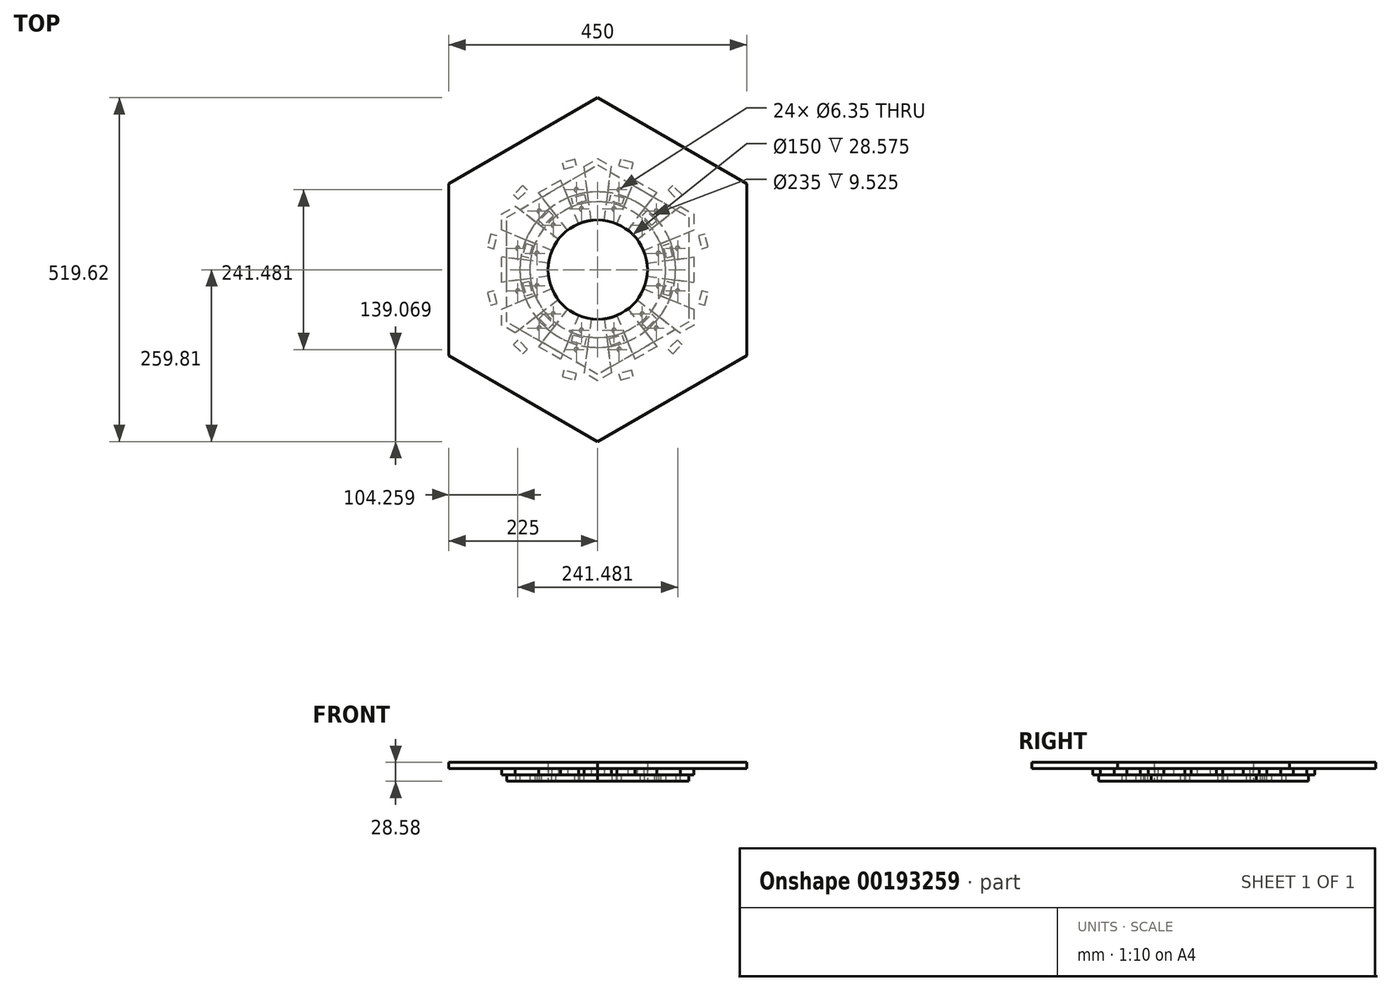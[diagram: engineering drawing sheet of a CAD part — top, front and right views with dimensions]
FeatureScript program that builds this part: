
annotation { "Feature Type Name" : "Feature", "Feature Type Description" : "" }
export const myFeature = defineFeature(function(context is Context, id is Id, definition is map)
    precondition{}
    {
        {
            var Q0;
            Q0=qCreatedBy(makeId("Top.planeOp"),FACE);
            var sketch = newSketch(context, id + "F0", { "sketchPlane" : qUnion([Q0])});
            skCircle(sketch, "E0.cCircle", {"center": v(0, 0) * mm, "radius": 158.5 * mm, "construction": true});
            skLineSegment(sketch, "E0.0", {"start": v(0, 158.5) * mm, "end": v(137.27, 79.25) * mm});
            skLineSegment(sketch, "E0.1", {"start": v(137.27, 79.25) * mm, "end": v(137.27, -79.25) * mm});
            skLineSegment(sketch, "E0.2", {"start": v(137.27, -79.25) * mm, "end": v(0, -158.5) * mm});
            skLineSegment(sketch, "E0.3", {"start": v(0, -158.5) * mm, "end": v(-137.27, -79.25) * mm});
            skLineSegment(sketch, "E0.4", {"start": v(-137.27, -79.25) * mm, "end": v(-137.27, 79.25) * mm});
            skLineSegment(sketch, "E0.5", {"start": v(-137.27, 79.25) * mm, "end": v(0, 158.5) * mm});
            skCircle(sketch, "E1", {"center": v(0, 0) * mm, "radius": 75 * mm});
            skLineSegment(sketch, "E2", {"start": v(0, 0) * mm, "end": v(0, 158.5) * mm});
            skLineSegment(sketch, "E3", {"start": v(0, 0) * mm, "end": v(24.59, 91.76) * mm});
            skLineSegment(sketch, "E4", {"start": v(32.35, 120.74) * mm, "end": v(24.59, 91.76) * mm});
            skCircle(sketch, "E5", {"center": v(24.59, 91.76) * mm, "radius": 3.18 * mm});
            skCircle(sketch, "E6", {"center": v(32.35, 120.74) * mm, "radius": 3.18 * mm});
            skCircle(sketch, "E7.1.0", {"center": v(-24.59, 91.76) * mm, "radius": 3.18 * mm});
            skCircle(sketch, "E7.1.1", {"center": v(-32.35, 120.74) * mm, "radius": 3.18 * mm});
            skCircle(sketch, "E7.2.0", {"center": v(-67.18, 67.18) * mm, "radius": 3.18 * mm});
            skCircle(sketch, "E7.2.1", {"center": v(-88.39, 88.39) * mm, "radius": 3.18 * mm});
            skCircle(sketch, "E7.3.0", {"center": v(-91.76, 24.59) * mm, "radius": 3.18 * mm});
            skCircle(sketch, "E7.3.1", {"center": v(-120.74, 32.35) * mm, "radius": 3.18 * mm});
            skCircle(sketch, "E7.4.0", {"center": v(-91.76, -24.59) * mm, "radius": 3.18 * mm});
            skCircle(sketch, "E7.4.1", {"center": v(-120.74, -32.35) * mm, "radius": 3.18 * mm});
            skCircle(sketch, "E7.5.0", {"center": v(-67.18, -67.18) * mm, "radius": 3.18 * mm});
            skCircle(sketch, "E7.5.1", {"center": v(-88.39, -88.39) * mm, "radius": 3.18 * mm});
            skCircle(sketch, "E7.6.0", {"center": v(-24.59, -91.76) * mm, "radius": 3.18 * mm});
            skCircle(sketch, "E7.6.1", {"center": v(-32.35, -120.74) * mm, "radius": 3.18 * mm});
            skCircle(sketch, "E7.7.0", {"center": v(24.59, -91.76) * mm, "radius": 3.18 * mm});
            skCircle(sketch, "E7.7.1", {"center": v(32.35, -120.74) * mm, "radius": 3.18 * mm});
            skCircle(sketch, "E7.8.0", {"center": v(67.18, -67.18) * mm, "radius": 3.18 * mm});
            skCircle(sketch, "E7.8.1", {"center": v(88.39, -88.39) * mm, "radius": 3.18 * mm});
            skCircle(sketch, "E7.9.0", {"center": v(91.76, -24.59) * mm, "radius": 3.18 * mm});
            skCircle(sketch, "E7.9.1", {"center": v(120.74, -32.35) * mm, "radius": 3.18 * mm});
            skCircle(sketch, "E7.10.0", {"center": v(91.76, 24.59) * mm, "radius": 3.18 * mm});
            skCircle(sketch, "E7.10.1", {"center": v(120.74, 32.35) * mm, "radius": 3.18 * mm});
            skCircle(sketch, "E7.11.0", {"center": v(67.18, 67.18) * mm, "radius": 3.18 * mm});
            skCircle(sketch, "E7.11.1", {"center": v(88.39, 88.39) * mm, "radius": 3.18 * mm});
            skSolve(sketch);
        }
        {
            var Q0;
            Q0 = qSketchRegion(id + "F0", true);
            extrude(context, id + "F1", {"entities" : qUnion([Q0]), "depth" : 9.53 * mm});
        }
        {
            var Q0;
            Q0=makeQuery(id+"F1.opExtrude","CAP_FACE",FACE,{"disambiguationData":[OSD([sQuery(id+"F0.wireOp",EDGE,"E0.0"),sQuery(id+"F0.wireOp",EDGE,"E0.1"),sQuery(id+"F0.wireOp",EDGE,"E0.2"),sQuery(id+"F0.wireOp",EDGE,"E0.3"),sQuery(id+"F0.wireOp",EDGE,"E0.4"),sQuery(id+"F0.wireOp",EDGE,"E0.5"),sQuery(id+"F0.wireOp",EDGE,"RleesNmM-tFlp-8cQn-oHbe-ywBhveo3HyHZ")])],"isStart":false});
            var sketch = newSketch(context, id + "F2", { "sketchPlane" : qUnion([Q0])});
            skCircle(sketch, "E8.cCircle", {"center": v(0, 0) * mm, "radius": 167.74 * mm, "construction": true});
            skLineSegment(sketch, "E8.0", {"start": v(145.27, -83.87) * mm, "end": v(0, -167.74) * mm});
            skLineSegment(sketch, "E8.1", {"start": v(0, -167.74) * mm, "end": v(-145.27, -83.87) * mm});
            skLineSegment(sketch, "E8.2", {"start": v(-145.27, -83.87) * mm, "end": v(-145.27, 83.87) * mm});
            skLineSegment(sketch, "E8.3", {"start": v(-145.27, 83.87) * mm, "end": v(0, 167.74) * mm});
            skLineSegment(sketch, "E8.4", {"start": v(0, 167.74) * mm, "end": v(145.27, 83.87) * mm});
            skLineSegment(sketch, "E8.5", {"start": v(145.27, 83.87) * mm, "end": v(145.27, -83.87) * mm});
            skLineSegment(sketch, "E9", {"start": v(0, 0) * mm, "end": v(167.74, 0) * mm});
            skLineSegment(sketch, "E10", {"start": v(0, 0) * mm, "end": v(166.3, -21.9) * mm});
            skLineSegment(sketch, "E11.1.0", {"start": v(0, 0) * mm, "end": v(166.3, 21.9) * mm});
            skLineSegment(sketch, "E11.2.0", {"start": v(0, 0) * mm, "end": v(154.97, 64.2) * mm});
            skLineSegment(sketch, "E11.3.0", {"start": v(0, 0) * mm, "end": v(133.08, 102.11) * mm});
            skLineSegment(sketch, "E11.4.0", {"start": v(0, 0) * mm, "end": v(102.11, 133.08) * mm});
            skLineSegment(sketch, "E11.5.0", {"start": v(0, 0) * mm, "end": v(64.2, 154.97) * mm});
            skLineSegment(sketch, "E11.7.0", {"start": v(0, 0) * mm, "end": v(-21.9, 166.3) * mm});
            skLineSegment(sketch, "E11.8.0", {"start": v(0, 0) * mm, "end": v(-64.2, 154.97) * mm});
            skLineSegment(sketch, "E11.9.0", {"start": v(0, 0) * mm, "end": v(-102.11, 133.08) * mm});
            skLineSegment(sketch, "E11.10.0", {"start": v(0, 0) * mm, "end": v(-133.08, 102.11) * mm});
            skLineSegment(sketch, "E11.11.0", {"start": v(0, 0) * mm, "end": v(-154.97, 64.2) * mm});
            skLineSegment(sketch, "E11.12.0", {"start": v(0, 0) * mm, "end": v(-166.3, 21.9) * mm});
            skLineSegment(sketch, "E11.13.0", {"start": v(0, 0) * mm, "end": v(-166.3, -21.9) * mm});
            skLineSegment(sketch, "E11.14.0", {"start": v(0, 0) * mm, "end": v(-154.97, -64.2) * mm});
            skLineSegment(sketch, "E11.15.0", {"start": v(0, 0) * mm, "end": v(-133.08, -102.11) * mm});
            skLineSegment(sketch, "E11.16.0", {"start": v(0, 0) * mm, "end": v(-102.11, -133.08) * mm});
            skLineSegment(sketch, "E11.17.0", {"start": v(0, 0) * mm, "end": v(-64.2, -154.97) * mm});
            skLineSegment(sketch, "E11.18.0", {"start": v(0, 0) * mm, "end": v(-21.9, -166.3) * mm});
            skLineSegment(sketch, "E11.19.0", {"start": v(0, 0) * mm, "end": v(21.9, -166.3) * mm});
            skLineSegment(sketch, "E11.20.0", {"start": v(0, 0) * mm, "end": v(64.2, -154.97) * mm});
            skLineSegment(sketch, "E11.21.0", {"start": v(0, 0) * mm, "end": v(102.11, -133.08) * mm});
            skLineSegment(sketch, "E11.22.0", {"start": v(0, 0) * mm, "end": v(133.08, -102.11) * mm});
            skLineSegment(sketch, "E11.23.0", {"start": v(0, 0) * mm, "end": v(154.97, -64.2) * mm});
            skCircle(sketch, "E12", {"center": v(0, 0) * mm, "radius": 75 * mm});
            skLineSegment(sketch, "E13", {"start": v(0, 0) * mm, "end": v(20.52, 155.89) * mm});
            skSolve(sketch);
        }
        {
            var Q0;
            {var subQ0=sQuery(id+"F2.wireOp",EDGE,"E11.5.0");var subQ1=sQuery(id+"F2.wireOp",EDGE,"E8.4");var subQ2=makeQuery(id+"F2.imprint","INTERSECT",VERTEX,{"derivedFrom":[subQ1,subQ0]});Q0=makeQuery(id+"F2.imprint","IMPRINT",FACE,{"disambiguationData":[TD([[makeQuery(id+"F2.imprint","IMPRINT",EDGE,{"disambiguationData":[TD([[subQ2,-1.0]])],"derivedFrom":subQ1}),-1.0]])]});}
            var Q1;
            {var subQ1=sQuery(id+"F2.wireOp",EDGE,"E8.3");var subQ6=sQuery(id+"F2.wireOp",EDGE,"E8.4");var subQ10=makeQuery(id+"F2.imprint","INTERSECT",VERTEX,{"derivedFrom":[subQ1,subQ6]});Q1=makeQuery(id+"F2.imprint","IMPRINT",FACE,{"disambiguationData":[TD([[makeQuery(id+"F2.imprint","IMPRINT",EDGE,{"disambiguationData":[TD([[subQ10,1.0]])],"derivedFrom":subQ1}),-1.0]])]});}
            var Q2;
            {var subQ0=sQuery(id+"F2.wireOp",EDGE,"E11.13.0");var subQ1=sQuery(id+"F2.wireOp",EDGE,"E8.2");var subQ2=makeQuery(id+"F2.imprint","INTERSECT",VERTEX,{"derivedFrom":[subQ1,subQ0]});Q2=makeQuery(id+"F2.imprint","IMPRINT",FACE,{"disambiguationData":[TD([[makeQuery(id+"F2.imprint","IMPRINT",EDGE,{"disambiguationData":[TD([[subQ2,-1.0]])],"derivedFrom":subQ1}),-1.0]])]});}
            var Q3;
            {var subQ1=sQuery(id+"F2.wireOp",EDGE,"E8.1");var subQ6=sQuery(id+"F2.wireOp",EDGE,"E8.2");var subQ10=makeQuery(id+"F2.imprint","INTERSECT",VERTEX,{"derivedFrom":[subQ1,subQ6]});Q3=makeQuery(id+"F2.imprint","IMPRINT",FACE,{"disambiguationData":[TD([[makeQuery(id+"F2.imprint","IMPRINT",EDGE,{"disambiguationData":[TD([[subQ10,1.0]])],"derivedFrom":subQ1}),-1.0]])]});}
            var Q4;
            {var subQ1=sQuery(id+"F2.wireOp",EDGE,"E8.0");var subQ6=sQuery(id+"F2.wireOp",EDGE,"E8.1");var subQ10=makeQuery(id+"F2.imprint","INTERSECT",VERTEX,{"derivedFrom":[subQ1,subQ6]});Q4=makeQuery(id+"F2.imprint","IMPRINT",FACE,{"disambiguationData":[TD([[makeQuery(id+"F2.imprint","IMPRINT",EDGE,{"disambiguationData":[TD([[subQ10,1.0]])],"derivedFrom":subQ1}),-1.0]])]});}
            var Q5;
            {var subQ0=sQuery(id+"F2.wireOp",EDGE,"E11.21.0");var subQ1=sQuery(id+"F2.wireOp",EDGE,"E8.0");var subQ2=makeQuery(id+"F2.imprint","INTERSECT",VERTEX,{"derivedFrom":[subQ1,subQ0]});Q5=makeQuery(id+"F2.imprint","IMPRINT",FACE,{"disambiguationData":[TD([[makeQuery(id+"F2.imprint","IMPRINT",EDGE,{"disambiguationData":[TD([[subQ2,-1.0]])],"derivedFrom":subQ1}),-1.0]])]});}
            var Q6;
            {var subQ1=sQuery(id+"F2.wireOp",EDGE,"E8.5");var subQ8=sQuery(id+"F2.wireOp",EDGE,"E8.0");var subQ11=makeQuery(id+"F2.imprint","INTERSECT",VERTEX,{"derivedFrom":[subQ8,subQ1]});Q6=makeQuery(id+"F2.imprint","IMPRINT",FACE,{"disambiguationData":[TD([[makeQuery(id+"F2.imprint","IMPRINT",EDGE,{"disambiguationData":[TD([[subQ11,-1.0]])],"derivedFrom":subQ8}),-1.0]])]});}
            var Q7;
            {var subQ1=sQuery(id+"F2.wireOp",EDGE,"E8.4");var subQ6=sQuery(id+"F2.wireOp",EDGE,"E8.5");var subQ10=makeQuery(id+"F2.imprint","INTERSECT",VERTEX,{"derivedFrom":[subQ1,subQ6]});Q7=makeQuery(id+"F2.imprint","IMPRINT",FACE,{"disambiguationData":[TD([[makeQuery(id+"F2.imprint","IMPRINT",EDGE,{"disambiguationData":[TD([[subQ10,1.0]])],"derivedFrom":subQ1}),-1.0]])]});}
            var Q8;
            {var subQ0=sQuery(id+"F2.wireOp",EDGE,"E11.5.0");var subQ1=sQuery(id+"F2.wireOp",EDGE,"E8.4");var subQ2=makeQuery(id+"F2.imprint","INTERSECT",VERTEX,{"derivedFrom":[subQ1,subQ0]});Q8=makeQuery(id+"F2.imprint","IMPRINT",FACE,{"disambiguationData":[TD([[makeQuery(id+"F2.imprint","IMPRINT",EDGE,{"disambiguationData":[TD([[subQ2,-1.0]])],"derivedFrom":subQ1}),-1.0]])]});}
            var Q9;
            {var subQ1=sQuery(id+"F2.wireOp",EDGE,"E8.3");var subQ5=sQuery(id+"F2.wireOp",EDGE,"E8.2");var subQ6=makeQuery(id+"F2.imprint","INTERSECT",VERTEX,{"derivedFrom":[subQ5,subQ1]});Q9=makeQuery(id+"F2.imprint","IMPRINT",FACE,{"disambiguationData":[TD([[makeQuery(id+"F2.imprint","IMPRINT",EDGE,{"disambiguationData":[TD([[subQ6,1.0]])],"derivedFrom":subQ5}),-1.0]])]});}
            var Q10;
            {var subQ5=sQuery(id+"F2.wireOp",EDGE,"E12");var subQ6=sQuery(id+"F2.wireOp",EDGE,"E11.10.0");var subQ7=makeQuery(id+"F2.imprint","INTERSECT",VERTEX,{"derivedFrom":[subQ6,subQ5]});Q10=makeQuery(id+"F2.imprint","IMPRINT",FACE,{"disambiguationData":[TD([[makeQuery(id+"F2.imprint","IMPRINT",EDGE,{"disambiguationData":[TD([[subQ7,-1.0]])],"derivedFrom":subQ6}),1.0]])]});}
            var Q11;
            {var subQ3=sQuery(id+"F2.wireOp",EDGE,"E11.6.0");var subQ5=sQuery(id+"F2.wireOp",EDGE,"E12");var subQ6=makeQuery(id+"F2.imprint","INTERSECT",VERTEX,{"derivedFrom":[subQ3,subQ5]});Q11=makeQuery(id+"F2.imprint","IMPRINT",FACE,{"disambiguationData":[TD([[makeQuery(id+"F2.imprint","IMPRINT",EDGE,{"disambiguationData":[TD([[subQ6,-1.0]])],"derivedFrom":subQ3}),1.0]])]});}
            var Q12;
            {var subQ0=sQuery(id+"F2.wireOp",EDGE,"E11.5.0");var subQ1=sQuery(id+"F2.wireOp",EDGE,"E8.4");var subQ2=makeQuery(id+"F2.imprint","INTERSECT",VERTEX,{"derivedFrom":[subQ1,subQ0]});Q12=makeQuery(id+"F2.imprint","IMPRINT",FACE,{"disambiguationData":[TD([[makeQuery(id+"F2.imprint","IMPRINT",EDGE,{"disambiguationData":[TD([[subQ2,-1.0]])],"derivedFrom":subQ1}),-1.0]])]});}
            var Q13;
            {var subQ0=sQuery(id+"F2.wireOp",EDGE,"E12");var subQ1=sQuery(id+"F2.wireOp",EDGE,"E11.4.0");var subQ2=makeQuery(id+"F2.imprint","INTERSECT",VERTEX,{"derivedFrom":[subQ1,subQ0]});Q13=makeQuery(id+"F2.imprint","IMPRINT",FACE,{"disambiguationData":[TD([[makeQuery(id+"F2.imprint","IMPRINT",EDGE,{"disambiguationData":[TD([[subQ2,-1.0]])],"derivedFrom":subQ1}),1.0]])]});}
            var Q14;
            {var subQ0=sQuery(id+"F2.wireOp",EDGE,"E11.4.0");var subQ1=makeQuery(id+"F1.opExtrude","CAP_EDGE",EDGE,{"disambiguationData":[OSD([sQuery(id+"F0.wireOp",EDGE,"ad7bd027-b6ec-4049-bcbc-d832936b2ed7.0")])],"isStart":false});var subQ2=makeQuery(id+"F2.imprint","INTERSECT",VERTEX,{"derivedFrom":[subQ1,subQ0]});Q14=makeQuery(id+"F2.imprint","IMPRINT",FACE,{"disambiguationData":[TD([[makeQuery(id+"F2.imprint","IMPRINT",EDGE,{"disambiguationData":[TD([[subQ2,-1.0]])],"derivedFrom":subQ0}),1.0]])]});}
            var Q15;
            {var subQ5=sQuery(id+"F2.wireOp",EDGE,"E12");var subQ6=sQuery(id+"F2.wireOp",EDGE,"E11.2.0");var subQ7=makeQuery(id+"F2.imprint","INTERSECT",VERTEX,{"derivedFrom":[subQ6,subQ5]});Q15=makeQuery(id+"F2.imprint","IMPRINT",FACE,{"disambiguationData":[TD([[makeQuery(id+"F2.imprint","IMPRINT",EDGE,{"disambiguationData":[TD([[subQ7,-1.0]])],"derivedFrom":subQ6}),1.0]])]});}
            var Q16;
            {var subQ5=sQuery(id+"F2.wireOp",EDGE,"E12");var subQ6=sQuery(id+"F2.wireOp",EDGE,"E11.22.0");var subQ7=makeQuery(id+"F2.imprint","INTERSECT",VERTEX,{"derivedFrom":[subQ6,subQ5]});Q16=makeQuery(id+"F2.imprint","IMPRINT",FACE,{"disambiguationData":[TD([[makeQuery(id+"F2.imprint","IMPRINT",EDGE,{"disambiguationData":[TD([[subQ7,-1.0]])],"derivedFrom":subQ6}),1.0]])]});}
            var Q17;
            {var subQ0=sQuery(id+"F2.wireOp",EDGE,"E11.21.0");var subQ1=sQuery(id+"F2.wireOp",EDGE,"E8.0");var subQ2=makeQuery(id+"F2.imprint","INTERSECT",VERTEX,{"derivedFrom":[subQ1,subQ0]});Q17=makeQuery(id+"F2.imprint","IMPRINT",FACE,{"disambiguationData":[TD([[makeQuery(id+"F2.imprint","IMPRINT",EDGE,{"disambiguationData":[TD([[subQ2,-1.0]])],"derivedFrom":subQ1}),-1.0]])]});}
            var Q18;
            {var subQ0=sQuery(id+"F2.wireOp",EDGE,"E12");var subQ1=sQuery(id+"F2.wireOp",EDGE,"E11.20.0");var subQ2=makeQuery(id+"F2.imprint","INTERSECT",VERTEX,{"derivedFrom":[subQ1,subQ0]});Q18=makeQuery(id+"F2.imprint","IMPRINT",FACE,{"disambiguationData":[TD([[makeQuery(id+"F2.imprint","IMPRINT",EDGE,{"disambiguationData":[TD([[subQ2,-1.0]])],"derivedFrom":subQ1}),1.0]])]});}
            var Q19;
            {var subQ0=sQuery(id+"F2.wireOp",EDGE,"E11.20.0");var subQ1=makeQuery(id+"F1.opExtrude","CAP_EDGE",EDGE,{"disambiguationData":[OSD([sQuery(id+"F0.wireOp",EDGE,"ad7bd027-b6ec-4049-bcbc-d832936b2ed7.2")])],"isStart":false});var subQ2=makeQuery(id+"F2.imprint","INTERSECT",VERTEX,{"derivedFrom":[subQ1,subQ0]});Q19=makeQuery(id+"F2.imprint","IMPRINT",FACE,{"disambiguationData":[TD([[makeQuery(id+"F2.imprint","IMPRINT",EDGE,{"disambiguationData":[TD([[subQ2,-1.0]])],"derivedFrom":subQ0}),1.0]])]});}
            var Q20;
            {var subQ5=sQuery(id+"F2.wireOp",EDGE,"E12");var subQ6=sQuery(id+"F2.wireOp",EDGE,"E11.18.0");var subQ7=makeQuery(id+"F2.imprint","INTERSECT",VERTEX,{"derivedFrom":[subQ6,subQ5]});Q20=makeQuery(id+"F2.imprint","IMPRINT",FACE,{"disambiguationData":[TD([[makeQuery(id+"F2.imprint","IMPRINT",EDGE,{"disambiguationData":[TD([[subQ7,-1.0]])],"derivedFrom":subQ6}),1.0]])]});}
            var Q21;
            {var subQ5=sQuery(id+"F2.wireOp",EDGE,"E12");var subQ6=sQuery(id+"F2.wireOp",EDGE,"E11.14.0");var subQ7=makeQuery(id+"F2.imprint","INTERSECT",VERTEX,{"derivedFrom":[subQ6,subQ5]});Q21=makeQuery(id+"F2.imprint","IMPRINT",FACE,{"disambiguationData":[TD([[makeQuery(id+"F2.imprint","IMPRINT",EDGE,{"disambiguationData":[TD([[subQ7,-1.0]])],"derivedFrom":subQ6}),1.0]])]});}
            var Q22;
            {var subQ0=sQuery(id+"F2.wireOp",EDGE,"E11.13.0");var subQ1=sQuery(id+"F2.wireOp",EDGE,"E8.2");var subQ2=makeQuery(id+"F2.imprint","INTERSECT",VERTEX,{"derivedFrom":[subQ1,subQ0]});Q22=makeQuery(id+"F2.imprint","IMPRINT",FACE,{"disambiguationData":[TD([[makeQuery(id+"F2.imprint","IMPRINT",EDGE,{"disambiguationData":[TD([[subQ2,-1.0]])],"derivedFrom":subQ1}),-1.0]])]});}
            var Q23;
            {var subQ0=sQuery(id+"F2.wireOp",EDGE,"E12");var subQ1=sQuery(id+"F2.wireOp",EDGE,"E11.12.0");var subQ2=makeQuery(id+"F2.imprint","INTERSECT",VERTEX,{"derivedFrom":[subQ1,subQ0]});Q23=makeQuery(id+"F2.imprint","IMPRINT",FACE,{"disambiguationData":[TD([[makeQuery(id+"F2.imprint","IMPRINT",EDGE,{"disambiguationData":[TD([[subQ2,-1.0]])],"derivedFrom":subQ1}),1.0]])]});}
            var Q24;
            {var subQ0=sQuery(id+"F2.wireOp",EDGE,"E11.12.0");var subQ1=makeQuery(id+"F1.opExtrude","CAP_EDGE",EDGE,{"disambiguationData":[OSD([sQuery(id+"F0.wireOp",EDGE,"ad7bd027-b6ec-4049-bcbc-d832936b2ed7.4")])],"isStart":false});var subQ2=makeQuery(id+"F2.imprint","INTERSECT",VERTEX,{"derivedFrom":[subQ1,subQ0]});Q24=makeQuery(id+"F2.imprint","IMPRINT",FACE,{"disambiguationData":[TD([[makeQuery(id+"F2.imprint","IMPRINT",EDGE,{"disambiguationData":[TD([[subQ2,-1.0]])],"derivedFrom":subQ0}),1.0]])]});}
            var Q25;
            {var subQ5=sQuery(id+"F2.wireOp",EDGE,"E12");var subQ6=sQuery(id+"F2.wireOp",EDGE,"E11.18.0");var subQ7=makeQuery(id+"F2.imprint","INTERSECT",VERTEX,{"derivedFrom":[subQ6,subQ5]});Q25=makeQuery(id+"F2.imprint","IMPRINT",FACE,{"disambiguationData":[TD([[makeQuery(id+"F2.imprint","IMPRINT",EDGE,{"disambiguationData":[TD([[subQ7,-1.0]])],"derivedFrom":subQ6}),1.0]])]});}
            var Q26;
            {var subQ5=sQuery(id+"F2.wireOp",EDGE,"E12");var subQ6=sQuery(id+"F2.wireOp",EDGE,"E11.14.0");var subQ7=makeQuery(id+"F2.imprint","INTERSECT",VERTEX,{"derivedFrom":[subQ6,subQ5]});Q26=makeQuery(id+"F2.imprint","IMPRINT",FACE,{"disambiguationData":[TD([[makeQuery(id+"F2.imprint","IMPRINT",EDGE,{"disambiguationData":[TD([[subQ7,-1.0]])],"derivedFrom":subQ6}),1.0]])]});}
            var Q27;
            {var subQ0=sQuery(id+"F2.wireOp",EDGE,"E12");var subQ1=sQuery(id+"F2.wireOp",EDGE,"E11.12.0");var subQ2=makeQuery(id+"F2.imprint","INTERSECT",VERTEX,{"derivedFrom":[subQ1,subQ0]});Q27=makeQuery(id+"F2.imprint","IMPRINT",FACE,{"disambiguationData":[TD([[makeQuery(id+"F2.imprint","IMPRINT",EDGE,{"disambiguationData":[TD([[subQ2,-1.0]])],"derivedFrom":subQ1}),1.0]])]});}
            var Q28;
            {var subQ5=sQuery(id+"F2.wireOp",EDGE,"E12");var subQ6=sQuery(id+"F2.wireOp",EDGE,"E11.10.0");var subQ7=makeQuery(id+"F2.imprint","INTERSECT",VERTEX,{"derivedFrom":[subQ6,subQ5]});Q28=makeQuery(id+"F2.imprint","IMPRINT",FACE,{"disambiguationData":[TD([[makeQuery(id+"F2.imprint","IMPRINT",EDGE,{"disambiguationData":[TD([[subQ7,-1.0]])],"derivedFrom":subQ6}),1.0]])]});}
            var Q29;
            {var subQ3=sQuery(id+"F2.wireOp",EDGE,"E11.6.0");var subQ5=sQuery(id+"F2.wireOp",EDGE,"E12");var subQ6=makeQuery(id+"F2.imprint","INTERSECT",VERTEX,{"derivedFrom":[subQ3,subQ5]});Q29=makeQuery(id+"F2.imprint","IMPRINT",FACE,{"disambiguationData":[TD([[makeQuery(id+"F2.imprint","IMPRINT",EDGE,{"disambiguationData":[TD([[subQ6,-1.0]])],"derivedFrom":subQ3}),1.0]])]});}
            var Q30;
            {var subQ0=sQuery(id+"F2.wireOp",EDGE,"E12");var subQ1=sQuery(id+"F2.wireOp",EDGE,"E11.4.0");var subQ2=makeQuery(id+"F2.imprint","INTERSECT",VERTEX,{"derivedFrom":[subQ1,subQ0]});Q30=makeQuery(id+"F2.imprint","IMPRINT",FACE,{"disambiguationData":[TD([[makeQuery(id+"F2.imprint","IMPRINT",EDGE,{"disambiguationData":[TD([[subQ2,-1.0]])],"derivedFrom":subQ1}),1.0]])]});}
            var Q31;
            {var subQ5=sQuery(id+"F2.wireOp",EDGE,"E12");var subQ6=sQuery(id+"F2.wireOp",EDGE,"E11.2.0");var subQ7=makeQuery(id+"F2.imprint","INTERSECT",VERTEX,{"derivedFrom":[subQ6,subQ5]});Q31=makeQuery(id+"F2.imprint","IMPRINT",FACE,{"disambiguationData":[TD([[makeQuery(id+"F2.imprint","IMPRINT",EDGE,{"disambiguationData":[TD([[subQ7,-1.0]])],"derivedFrom":subQ6}),1.0]])]});}
            var Q32;
            {var subQ5=sQuery(id+"F2.wireOp",EDGE,"E12");var subQ6=sQuery(id+"F2.wireOp",EDGE,"E11.22.0");var subQ7=makeQuery(id+"F2.imprint","INTERSECT",VERTEX,{"derivedFrom":[subQ6,subQ5]});Q32=makeQuery(id+"F2.imprint","IMPRINT",FACE,{"disambiguationData":[TD([[makeQuery(id+"F2.imprint","IMPRINT",EDGE,{"disambiguationData":[TD([[subQ7,-1.0]])],"derivedFrom":subQ6}),1.0]])]});}
            var Q33;
            {var subQ0=sQuery(id+"F2.wireOp",EDGE,"E12");var subQ1=sQuery(id+"F2.wireOp",EDGE,"E11.20.0");var subQ2=makeQuery(id+"F2.imprint","INTERSECT",VERTEX,{"derivedFrom":[subQ1,subQ0]});Q33=makeQuery(id+"F2.imprint","IMPRINT",FACE,{"disambiguationData":[TD([[makeQuery(id+"F2.imprint","IMPRINT",EDGE,{"disambiguationData":[TD([[subQ2,-1.0]])],"derivedFrom":subQ1}),1.0]])]});}
            var Q34;
            {var subQ5=sQuery(id+"F2.wireOp",EDGE,"E11.6.0");var subQ7=makeQuery(id+"F1.opExtrude","CAP_EDGE",EDGE,{"disambiguationData":[OSD([sQuery(id+"F0.wireOp",EDGE,"ad7bd027-b6ec-4049-bcbc-d832936b2ed7.0")])],"isStart":false});var subQ8=makeQuery(id+"F2.imprint","INTERSECT",VERTEX,{"derivedFrom":[subQ7,subQ5]});Q34=makeQuery(id+"F2.imprint","IMPRINT",FACE,{"disambiguationData":[TD([[makeQuery(id+"F2.imprint","IMPRINT",EDGE,{"disambiguationData":[TD([[subQ8,-1.0]])],"derivedFrom":subQ5}),1.0]])]});}
            var Q35;
            {var subQ3=sQuery(id+"F2.wireOp",EDGE,"E11.10.0");var subQ9=makeQuery(id+"F1.opExtrude","CAP_EDGE",EDGE,{"disambiguationData":[OSD([sQuery(id+"F0.wireOp",EDGE,"ad7bd027-b6ec-4049-bcbc-d832936b2ed7.5")])],"isStart":false});var subQ10=makeQuery(id+"F2.imprint","INTERSECT",VERTEX,{"derivedFrom":[subQ9,subQ3]});Q35=makeQuery(id+"F2.imprint","IMPRINT",FACE,{"disambiguationData":[TD([[makeQuery(id+"F2.imprint","IMPRINT",EDGE,{"disambiguationData":[TD([[subQ10,-1.0]])],"derivedFrom":subQ3}),1.0]])]});}
            var Q36;
            {var subQ7=sQuery(id+"F2.wireOp",EDGE,"E11.14.0");var subQ9=makeQuery(id+"F1.opExtrude","CAP_EDGE",EDGE,{"disambiguationData":[OSD([sQuery(id+"F0.wireOp",EDGE,"ad7bd027-b6ec-4049-bcbc-d832936b2ed7.4")])],"isStart":false});var subQ11=makeQuery(id+"F2.imprint","INTERSECT",VERTEX,{"derivedFrom":[subQ9,subQ7]});Q36=makeQuery(id+"F2.imprint","IMPRINT",FACE,{"disambiguationData":[TD([[makeQuery(id+"F2.imprint","IMPRINT",EDGE,{"disambiguationData":[TD([[subQ11,-1.0]])],"derivedFrom":subQ7}),1.0]])]});}
            var Q37;
            {var subQ7=makeQuery(id+"F1.opExtrude","CAP_EDGE",EDGE,{"disambiguationData":[OSD([sQuery(id+"F0.wireOp",EDGE,"ad7bd027-b6ec-4049-bcbc-d832936b2ed7.3")])],"isStart":false});var subQ9=sQuery(id+"F2.wireOp",EDGE,"E11.18.0");var subQ10=makeQuery(id+"F2.imprint","INTERSECT",VERTEX,{"derivedFrom":[subQ7,subQ9]});Q37=makeQuery(id+"F2.imprint","IMPRINT",FACE,{"disambiguationData":[TD([[makeQuery(id+"F2.imprint","IMPRINT",EDGE,{"disambiguationData":[TD([[subQ10,-1.0]])],"derivedFrom":subQ9}),1.0]])]});}
            var Q38;
            {var subQ5=makeQuery(id+"F1.opExtrude","CAP_EDGE",EDGE,{"disambiguationData":[OSD([sQuery(id+"F0.wireOp",EDGE,"ad7bd027-b6ec-4049-bcbc-d832936b2ed7.2")])],"isStart":false});var subQ9=sQuery(id+"F2.wireOp",EDGE,"E11.22.0");var subQ11=makeQuery(id+"F2.imprint","INTERSECT",VERTEX,{"derivedFrom":[subQ5,subQ9]});Q38=makeQuery(id+"F2.imprint","IMPRINT",FACE,{"disambiguationData":[TD([[makeQuery(id+"F2.imprint","IMPRINT",EDGE,{"disambiguationData":[TD([[subQ11,-1.0]])],"derivedFrom":subQ9}),1.0]])]});}
            var Q39;
            {var subQ3=sQuery(id+"F2.wireOp",EDGE,"E11.2.0");var subQ7=makeQuery(id+"F1.opExtrude","CAP_EDGE",EDGE,{"disambiguationData":[OSD([sQuery(id+"F0.wireOp",EDGE,"ad7bd027-b6ec-4049-bcbc-d832936b2ed7.1")])],"isStart":false});var subQ11=makeQuery(id+"F2.imprint","INTERSECT",VERTEX,{"derivedFrom":[subQ7,subQ3]});Q39=makeQuery(id+"F2.imprint","IMPRINT",FACE,{"disambiguationData":[TD([[makeQuery(id+"F2.imprint","IMPRINT",EDGE,{"disambiguationData":[TD([[subQ11,-1.0]])],"derivedFrom":subQ3}),1.0]])]});}
            var Q40;
            {var subQ0=sQuery(id+"F2.wireOp",EDGE,"E12");var subQ1=sQuery(id+"F2.wireOp",EDGE,"E9");var subQ2=makeQuery(id+"F2.imprint","INTERSECT",VERTEX,{"derivedFrom":[subQ1,subQ0]});Q40=makeQuery(id+"F2.imprint","IMPRINT",FACE,{"disambiguationData":[TD([[makeQuery(id+"F2.imprint","IMPRINT",EDGE,{"disambiguationData":[TD([[subQ2,-1.0]])],"derivedFrom":subQ1}),1.0]])]});}
            var Q41;
            {var subQ0=sQuery(id+"F2.wireOp",EDGE,"E12");var subQ1=sQuery(id+"F2.wireOp",EDGE,"E9");var subQ2=makeQuery(id+"F2.imprint","INTERSECT",VERTEX,{"derivedFrom":[subQ1,subQ0]});Q41=makeQuery(id+"F2.imprint","IMPRINT",FACE,{"disambiguationData":[TD([[makeQuery(id+"F2.imprint","IMPRINT",EDGE,{"disambiguationData":[TD([[subQ2,-1.0]])],"derivedFrom":subQ1}),-1.0]])]});}
            var Q42;
            {var subQ0=sQuery(id+"F2.wireOp",EDGE,"E9");var subQ1=makeQuery(id+"F1.opExtrude","CAP_EDGE",EDGE,{"disambiguationData":[OSD([sQuery(id+"F0.wireOp",EDGE,"ad7bd027-b6ec-4049-bcbc-d832936b2ed7.1")])],"isStart":false});var subQ2=makeQuery(id+"F2.imprint","INTERSECT",VERTEX,{"derivedFrom":[subQ1,subQ0]});Q42=makeQuery(id+"F2.imprint","IMPRINT",FACE,{"disambiguationData":[TD([[makeQuery(id+"F2.imprint","IMPRINT",EDGE,{"disambiguationData":[TD([[subQ2,-1.0]])],"derivedFrom":subQ0}),1.0]])]});}
            var Q43;
            {var subQ0=sQuery(id+"F2.wireOp",EDGE,"E9");var subQ1=makeQuery(id+"F1.opExtrude","CAP_EDGE",EDGE,{"disambiguationData":[OSD([sQuery(id+"F0.wireOp",EDGE,"ad7bd027-b6ec-4049-bcbc-d832936b2ed7.1")])],"isStart":false});var subQ2=makeQuery(id+"F2.imprint","INTERSECT",VERTEX,{"derivedFrom":[subQ1,subQ0]});Q43=makeQuery(id+"F2.imprint","IMPRINT",FACE,{"disambiguationData":[TD([[makeQuery(id+"F2.imprint","IMPRINT",EDGE,{"disambiguationData":[TD([[subQ2,-1.0]])],"derivedFrom":subQ0}),-1.0]])]});}
            var Q44;
            {var subQ0=sQuery(id+"F2.wireOp",EDGE,"E11.1.0");var subQ1=sQuery(id+"F2.wireOp",EDGE,"E8.5");var subQ2=makeQuery(id+"F2.imprint","INTERSECT",VERTEX,{"derivedFrom":[subQ1,subQ0]});Q44=makeQuery(id+"F2.imprint","IMPRINT",FACE,{"disambiguationData":[TD([[makeQuery(id+"F2.imprint","IMPRINT",EDGE,{"disambiguationData":[TD([[subQ2,-1.0]])],"derivedFrom":subQ1}),-1.0]])]});}
            var Q45;
            {var subQ0=sQuery(id+"F2.wireOp",EDGE,"E9");var subQ1=sQuery(id+"F2.wireOp",EDGE,"E8.5");var subQ2=makeQuery(id+"F2.imprint","INTERSECT",VERTEX,{"derivedFrom":[subQ1,subQ0]});Q45=makeQuery(id+"F2.imprint","IMPRINT",FACE,{"disambiguationData":[TD([[makeQuery(id+"F2.imprint","IMPRINT",EDGE,{"disambiguationData":[TD([[subQ2,-1.0]])],"derivedFrom":subQ1}),-1.0]])]});}
            var Q46;
            {var subQ0=sQuery(id+"F2.wireOp",EDGE,"E11.16.0");var subQ1=makeQuery(id+"F1.opExtrude","CAP_EDGE",EDGE,{"disambiguationData":[OSD([sQuery(id+"F0.wireOp",EDGE,"ad7bd027-b6ec-4049-bcbc-d832936b2ed7.3")])],"isStart":false});var subQ2=makeQuery(id+"F2.imprint","INTERSECT",VERTEX,{"derivedFrom":[subQ1,subQ0]});Q46=makeQuery(id+"F2.imprint","IMPRINT",FACE,{"disambiguationData":[TD([[makeQuery(id+"F2.imprint","IMPRINT",EDGE,{"disambiguationData":[TD([[subQ2,-1.0]])],"derivedFrom":subQ0}),1.0]])]});}
            var Q47;
            {var subQ0=sQuery(id+"F2.wireOp",EDGE,"E11.17.0");var subQ1=sQuery(id+"F2.wireOp",EDGE,"E8.1");var subQ2=makeQuery(id+"F2.imprint","INTERSECT",VERTEX,{"derivedFrom":[subQ1,subQ0]});Q47=makeQuery(id+"F2.imprint","IMPRINT",FACE,{"disambiguationData":[TD([[makeQuery(id+"F2.imprint","IMPRINT",EDGE,{"disambiguationData":[TD([[subQ2,-1.0]])],"derivedFrom":subQ1}),-1.0]])]});}
            var Q48;
            {var subQ0=sQuery(id+"F2.wireOp",EDGE,"E12");var subQ1=sQuery(id+"F2.wireOp",EDGE,"E11.16.0");var subQ2=makeQuery(id+"F2.imprint","INTERSECT",VERTEX,{"derivedFrom":[subQ1,subQ0]});Q48=makeQuery(id+"F2.imprint","IMPRINT",FACE,{"disambiguationData":[TD([[makeQuery(id+"F2.imprint","IMPRINT",EDGE,{"disambiguationData":[TD([[subQ2,-1.0]])],"derivedFrom":subQ1}),1.0]])]});}
            var Q49;
            {var subQ0=sQuery(id+"F2.wireOp",EDGE,"E11.9.0");var subQ1=sQuery(id+"F2.wireOp",EDGE,"E8.3");var subQ2=makeQuery(id+"F2.imprint","INTERSECT",VERTEX,{"derivedFrom":[subQ1,subQ0]});Q49=makeQuery(id+"F2.imprint","IMPRINT",FACE,{"disambiguationData":[TD([[makeQuery(id+"F2.imprint","IMPRINT",EDGE,{"disambiguationData":[TD([[subQ2,-1.0]])],"derivedFrom":subQ1}),-1.0]])]});}
            var Q50;
            {var subQ0=sQuery(id+"F2.wireOp",EDGE,"E11.8.0");var subQ1=makeQuery(id+"F1.opExtrude","CAP_EDGE",EDGE,{"disambiguationData":[OSD([sQuery(id+"F0.wireOp",EDGE,"ad7bd027-b6ec-4049-bcbc-d832936b2ed7.5")])],"isStart":false});var subQ2=makeQuery(id+"F2.imprint","INTERSECT",VERTEX,{"derivedFrom":[subQ1,subQ0]});Q50=makeQuery(id+"F2.imprint","IMPRINT",FACE,{"disambiguationData":[TD([[makeQuery(id+"F2.imprint","IMPRINT",EDGE,{"disambiguationData":[TD([[subQ2,-1.0]])],"derivedFrom":subQ0}),1.0]])]});}
            var Q51;
            {var subQ0=sQuery(id+"F2.wireOp",EDGE,"E12");var subQ1=sQuery(id+"F2.wireOp",EDGE,"E11.8.0");var subQ2=makeQuery(id+"F2.imprint","INTERSECT",VERTEX,{"derivedFrom":[subQ1,subQ0]});Q51=makeQuery(id+"F2.imprint","IMPRINT",FACE,{"disambiguationData":[TD([[makeQuery(id+"F2.imprint","IMPRINT",EDGE,{"disambiguationData":[TD([[subQ2,-1.0]])],"derivedFrom":subQ1}),1.0]])]});}
            var Q52;
            {var subQ5=makeQuery(id+"F1.opExtrude","CAP_EDGE",EDGE,{"disambiguationData":[OSD([sQuery(id+"F0.wireOp",EDGE,"E1")])],"isStart":false});var subQ7=sQuery(id+"F2.wireOp",EDGE,"E11.18.0");var subQ8=makeQuery(id+"F2.imprint","INTERSECT",VERTEX,{"derivedFrom":[subQ5,subQ7]});Q52=makeQuery(id+"F2.imprint","IMPRINT",FACE,{"disambiguationData":[TD([[makeQuery(id+"F2.imprint","IMPRINT",EDGE,{"disambiguationData":[TD([[subQ8,-1.0]])],"derivedFrom":subQ7}),1.0]])]});}
            var Q53;
            {var subQ5=sQuery(id+"F2.wireOp",EDGE,"E11.22.0");var subQ7=makeQuery(id+"F1.opExtrude","CAP_EDGE",EDGE,{"disambiguationData":[OSD([sQuery(id+"F0.wireOp",EDGE,"E1")])],"isStart":false});var subQ9=makeQuery(id+"F2.imprint","INTERSECT",VERTEX,{"derivedFrom":[subQ7,subQ5]});Q53=makeQuery(id+"F2.imprint","IMPRINT",FACE,{"disambiguationData":[TD([[makeQuery(id+"F2.imprint","IMPRINT",EDGE,{"disambiguationData":[TD([[subQ9,-1.0]])],"derivedFrom":subQ5}),1.0]])]});}
            var Q54;
            {var subQ3=sQuery(id+"F2.wireOp",EDGE,"E11.2.0");var subQ7=makeQuery(id+"F1.opExtrude","CAP_EDGE",EDGE,{"disambiguationData":[OSD([sQuery(id+"F0.wireOp",EDGE,"E1")])],"isStart":false});var subQ9=makeQuery(id+"F2.imprint","INTERSECT",VERTEX,{"derivedFrom":[subQ7,subQ3]});Q54=makeQuery(id+"F2.imprint","IMPRINT",FACE,{"disambiguationData":[TD([[makeQuery(id+"F2.imprint","IMPRINT",EDGE,{"disambiguationData":[TD([[subQ9,-1.0]])],"derivedFrom":subQ3}),1.0]])]});}
            var Q55;
            {var subQ5=sQuery(id+"F2.wireOp",EDGE,"E11.6.0");var subQ7=makeQuery(id+"F1.opExtrude","CAP_EDGE",EDGE,{"disambiguationData":[OSD([sQuery(id+"F0.wireOp",EDGE,"E1")])],"isStart":false});var subQ8=makeQuery(id+"F2.imprint","INTERSECT",VERTEX,{"derivedFrom":[subQ7,subQ5]});Q55=makeQuery(id+"F2.imprint","IMPRINT",FACE,{"disambiguationData":[TD([[makeQuery(id+"F2.imprint","IMPRINT",EDGE,{"disambiguationData":[TD([[subQ8,-1.0]])],"derivedFrom":subQ5}),1.0]])]});}
            var Q56;
            {var subQ3=sQuery(id+"F2.wireOp",EDGE,"E11.10.0");var subQ7=makeQuery(id+"F1.opExtrude","CAP_EDGE",EDGE,{"disambiguationData":[OSD([sQuery(id+"F0.wireOp",EDGE,"E1")])],"isStart":false});var subQ8=makeQuery(id+"F2.imprint","INTERSECT",VERTEX,{"derivedFrom":[subQ7,subQ3]});Q56=makeQuery(id+"F2.imprint","IMPRINT",FACE,{"disambiguationData":[TD([[makeQuery(id+"F2.imprint","IMPRINT",EDGE,{"disambiguationData":[TD([[subQ8,-1.0]])],"derivedFrom":subQ3}),1.0]])]});}
            var Q57;
            {var subQ1=makeQuery(id+"F1.opExtrude","CAP_EDGE",EDGE,{"disambiguationData":[OSD([sQuery(id+"F0.wireOp",EDGE,"E1")])],"isStart":false});var subQ7=sQuery(id+"F2.wireOp",EDGE,"E11.14.0");var subQ9=makeQuery(id+"F2.imprint","INTERSECT",VERTEX,{"derivedFrom":[subQ1,subQ7]});Q57=makeQuery(id+"F2.imprint","IMPRINT",FACE,{"disambiguationData":[TD([[makeQuery(id+"F2.imprint","IMPRINT",EDGE,{"disambiguationData":[TD([[subQ9,-1.0]])],"derivedFrom":subQ7}),1.0]])]});}
            var Q58;
            {var subQ1=sQuery(id+"F2.wireOp",EDGE,"E12");var subQ5=sQuery(id+"F2.wireOp",EDGE,"E11.7.0");var subQ6=makeQuery(id+"F2.imprint","INTERSECT",VERTEX,{"derivedFrom":[subQ5,subQ1]});Q58=makeQuery(id+"F2.imprint","IMPRINT",FACE,{"disambiguationData":[TD([[makeQuery(id+"F2.imprint","IMPRINT",EDGE,{"disambiguationData":[TD([[subQ6,-1.0]])],"derivedFrom":subQ5}),-1.0]])]});}
            extrude(context, id + "F3", {"entities" : qUnion([Q0, Q1, Q2, Q3, Q4, Q5, Q6, Q7, Q8, Q9, Q10, Q11, Q12, Q13, Q14, Q15, Q16, Q17, Q18, Q19, Q20, Q21, Q22, Q23, Q24, Q25, Q26, Q27, Q28, Q29, Q30, Q31, Q32, Q33, Q34, Q35, Q36, Q37, Q38, Q39, Q40, Q41, Q42, Q43, Q44, Q45, Q46, Q47, Q48, Q49, Q50, Q51, Q52, Q53, Q54, Q55, Q56, Q57, Q58]), "operationType" : NewBodyOperationType.ADD, "depth" : 9.53 * mm});
        }
        {
            var Q0;
            Q0=makeQuery(id+"F3.opExtrude","CAP_FACE",FACE,{"disambiguationData":[OSD([sQuery(id+"F0.wireOp",EDGE,"RleesNmM-tFlp-8cQn-oHbe-ywBhveo3HyHZ"),sQuery(id+"F2.wireOp",EDGE,"E8.3"),sQuery(id+"F2.wireOp",EDGE,"E8.4"),sQuery(id+"F2.wireOp",EDGE,"E11.6.0"),sQuery(id+"F2.wireOp",EDGE,"E11.7.0")])],"isStart":false});
            var sketch = newSketch(context, id + "F4", { "sketchPlane" : qUnion([Q0])});
            skCircle(sketch, "E14.cCircle", {"center": v(0, 0) * mm, "radius": 259.8 * mm, "construction": true});
            skLineSegment(sketch, "E14.0", {"start": v(0, 259.8) * mm, "end": v(225, 129.9) * mm});
            skLineSegment(sketch, "E14.1", {"start": v(225, 129.9) * mm, "end": v(225, -129.9) * mm});
            skLineSegment(sketch, "E14.2", {"start": v(225, -129.9) * mm, "end": v(0, -259.8) * mm});
            skLineSegment(sketch, "E14.3", {"start": v(0, -259.8) * mm, "end": v(-225, -129.9) * mm});
            skLineSegment(sketch, "E14.4", {"start": v(-225, -129.9) * mm, "end": v(-225, 129.9) * mm});
            skLineSegment(sketch, "E14.5", {"start": v(-225, 129.9) * mm, "end": v(0, 259.8) * mm});
            skLineSegment(sketch, "E15", {"start": v(0, 0) * mm, "end": v(0, 75) * mm});
            skCircle(sketch, "E16", {"center": v(0, 0) * mm, "radius": 75 * mm});
            skLineSegment(sketch, "E17", {"start": v(0, 0) * mm, "end": v(-27.18, 101.42) * mm});
            skLineSegment(sketch, "E18", {"start": v(-27.18, 101.42) * mm, "end": v(-31.06, 115.91) * mm});
            skSolve(sketch);
        }
        {
            var Q0;
            Q0=makeQuery(id+"F4.imprint","IMPRINT",FACE,{"disambiguationData":[TD([[makeQuery(id+"F4.imprint","IMPRINT",EDGE,{"derivedFrom":sQuery(id+"F4.wireOp",EDGE,"E14.0")}),-1.0]])]});
            var Q1;
            {var subQ1=sQuery(id+"F2.wireOp",EDGE,"E11.6.0");Q1=makeQuery(id+"F4.imprint","IMPRINT",FACE,{"disambiguationData":[TD([[makeQuery(id+"F4.imprint","IMPRINT",EDGE,{"derivedFrom":makeQuery(id+"F3.opExtrude","CAP_EDGE",EDGE,{"disambiguationData":[OSD([subQ1])],"isStart":false})}),1.0]])]});}
            var Q2;
            {var subQ4=sQuery(id+"F2.wireOp",EDGE,"E11.7.0");var subQ6=makeQuery(id+"F3.opExtrude","CAP_EDGE",EDGE,{"disambiguationData":[OSD([subQ4])],"isStart":false});Q2=makeQuery(id+"F4.imprint","IMPRINT",FACE,{"disambiguationData":[TD([[makeQuery(id+"F4.imprint","IMPRINT",EDGE,{"derivedFrom":subQ6}),-1.0]])]});}
            extrude(context, id + "F5", {"entities" : qUnion([Q0, Q1, Q2]), "operationType" : NewBodyOperationType.ADD, "depth" : 9.53 * mm});
        }
        {
            var Q0;
            Q0=makeQuery(id+"F5.opExtrude","CAP_FACE",FACE,{"disambiguationData":[OSD([sQuery(id+"F4.wireOp",EDGE,"E14.0"),sQuery(id+"F4.wireOp",EDGE,"E14.1"),sQuery(id+"F4.wireOp",EDGE,"E14.2"),sQuery(id+"F4.wireOp",EDGE,"E14.3"),sQuery(id+"F4.wireOp",EDGE,"E14.4"),sQuery(id+"F4.wireOp",EDGE,"E14.5"),sQuery(id+"F4.wireOp",EDGE,"E16")])],"isStart":true});
            var sketch = newSketch(context, id + "F6", { "sketchPlane" : qUnion([Q0])});
            skLineSegment(sketch, "E19", {"start": v(0, 0) * mm, "end": v(0, 259.8) * mm});
            skLineSegment(sketch, "E20", {"start": v(17.52, 104.01) * mm, "end": v(36.84, 98.83) * mm});
            skLineSegment(sketch, "E21", {"start": v(0, 0) * mm, "end": v(27.18, 101.42) * mm});
            skLineSegment(sketch, "E22", {"start": v(20.1, 113.67) * mm, "end": v(39.42, 108.5) * mm});
            skLineSegment(sketch, "E23", {"start": v(20.1, 113.67) * mm, "end": v(17.52, 104.01) * mm});
            skLineSegment(sketch, "E24", {"start": v(36.84, 98.83) * mm, "end": v(39.42, 108.5) * mm});
            skLineSegment(sketch, "E25", {"start": v(29.76, 111.08) * mm, "end": v(41.41, 154.55) * mm});
            skLineSegment(sketch, "E26", {"start": v(34.34, 166.8) * mm, "end": v(53.66, 161.62) * mm});
            skLineSegment(sketch, "E27", {"start": v(53.66, 161.62) * mm, "end": v(51.07, 151.96) * mm});
            skLineSegment(sketch, "E28", {"start": v(51.07, 151.96) * mm, "end": v(31.75, 157.14) * mm});
            skLineSegment(sketch, "E29", {"start": v(31.75, 157.14) * mm, "end": v(34.34, 166.8) * mm});
            skLineSegment(sketch, "E30", {"start": v(29.76, 111.08) * mm, "end": v(22, 82.1) * mm});
            skPoint(sketch, "E31.center", {"position": v(0, 0) * mm});
            skLineSegment(sketch, "E32.1.0", {"start": v(-31.75, 157.14) * mm, "end": v(-51.07, 151.96) * mm});
            skLineSegment(sketch, "E32.1.1", {"start": v(-36.84, 98.83) * mm, "end": v(-17.52, 104.01) * mm});
            skLineSegment(sketch, "E32.1.2", {"start": v(-51.07, 151.96) * mm, "end": v(-53.66, 161.62) * mm});
            skLineSegment(sketch, "E32.1.3", {"start": v(-17.52, 104.01) * mm, "end": v(-20.1, 113.67) * mm});
            skLineSegment(sketch, "E32.1.4", {"start": v(-39.42, 108.5) * mm, "end": v(-20.1, 113.67) * mm});
            skLineSegment(sketch, "E32.1.5", {"start": v(-39.42, 108.5) * mm, "end": v(-36.84, 98.83) * mm});
            skLineSegment(sketch, "E32.1.6", {"start": v(-34.34, 166.8) * mm, "end": v(-31.75, 157.14) * mm});
            skLineSegment(sketch, "E32.1.7", {"start": v(-29.76, 111.08) * mm, "end": v(-22, 82.1) * mm});
            skLineSegment(sketch, "E32.1.8", {"start": v(-53.66, 161.62) * mm, "end": v(-34.34, 166.8) * mm});
            skLineSegment(sketch, "E32.2.0", {"start": v(-106.07, 120.2) * mm, "end": v(-120.2, 106.07) * mm});
            skLineSegment(sketch, "E32.2.1", {"start": v(-81.32, 67.18) * mm, "end": v(-67.18, 81.32) * mm});
            skLineSegment(sketch, "E32.2.2", {"start": v(-120.2, 106.07) * mm, "end": v(-127.28, 113.14) * mm});
            skLineSegment(sketch, "E32.2.3", {"start": v(-67.18, 81.32) * mm, "end": v(-74.25, 88.39) * mm});
            skLineSegment(sketch, "E32.2.4", {"start": v(-88.39, 74.25) * mm, "end": v(-74.25, 88.39) * mm});
            skLineSegment(sketch, "E32.2.5", {"start": v(-88.39, 74.25) * mm, "end": v(-81.32, 67.18) * mm});
            skLineSegment(sketch, "E32.2.6", {"start": v(-113.14, 127.28) * mm, "end": v(-106.07, 120.2) * mm});
            skLineSegment(sketch, "E32.2.7", {"start": v(-81.32, 81.32) * mm, "end": v(-60.1, 60.1) * mm});
            skLineSegment(sketch, "E32.2.8", {"start": v(-127.28, 113.14) * mm, "end": v(-113.14, 127.28) * mm});
            skLineSegment(sketch, "E32.3.0", {"start": v(-151.96, 51.07) * mm, "end": v(-157.14, 31.75) * mm});
            skLineSegment(sketch, "E32.3.1", {"start": v(-104.01, 17.52) * mm, "end": v(-98.83, 36.84) * mm});
            skLineSegment(sketch, "E32.3.2", {"start": v(-157.14, 31.75) * mm, "end": v(-166.8, 34.34) * mm});
            skLineSegment(sketch, "E32.3.3", {"start": v(-98.83, 36.84) * mm, "end": v(-108.5, 39.42) * mm});
            skLineSegment(sketch, "E32.3.4", {"start": v(-113.67, 20.1) * mm, "end": v(-108.5, 39.42) * mm});
            skLineSegment(sketch, "E32.3.5", {"start": v(-113.67, 20.1) * mm, "end": v(-104.01, 17.52) * mm});
            skLineSegment(sketch, "E32.3.6", {"start": v(-161.62, 53.66) * mm, "end": v(-151.96, 51.07) * mm});
            skLineSegment(sketch, "E32.3.7", {"start": v(-111.08, 29.76) * mm, "end": v(-82.1, 22) * mm});
            skLineSegment(sketch, "E32.3.8", {"start": v(-166.8, 34.34) * mm, "end": v(-161.62, 53.66) * mm});
            skLineSegment(sketch, "E32.4.0", {"start": v(-157.14, -31.75) * mm, "end": v(-151.96, -51.07) * mm});
            skLineSegment(sketch, "E32.4.1", {"start": v(-98.83, -36.84) * mm, "end": v(-104.01, -17.52) * mm});
            skLineSegment(sketch, "E32.4.2", {"start": v(-151.96, -51.07) * mm, "end": v(-161.62, -53.66) * mm});
            skLineSegment(sketch, "E32.4.3", {"start": v(-104.01, -17.52) * mm, "end": v(-113.67, -20.1) * mm});
            skLineSegment(sketch, "E32.4.4", {"start": v(-108.5, -39.42) * mm, "end": v(-113.67, -20.1) * mm});
            skLineSegment(sketch, "E32.4.5", {"start": v(-108.5, -39.42) * mm, "end": v(-98.83, -36.84) * mm});
            skLineSegment(sketch, "E32.4.6", {"start": v(-166.8, -34.34) * mm, "end": v(-157.14, -31.75) * mm});
            skLineSegment(sketch, "E32.4.7", {"start": v(-111.08, -29.76) * mm, "end": v(-82.1, -22) * mm});
            skLineSegment(sketch, "E32.4.8", {"start": v(-161.62, -53.66) * mm, "end": v(-166.8, -34.34) * mm});
            skLineSegment(sketch, "E32.5.0", {"start": v(-120.2, -106.07) * mm, "end": v(-106.07, -120.2) * mm});
            skLineSegment(sketch, "E32.5.1", {"start": v(-67.18, -81.32) * mm, "end": v(-81.32, -67.18) * mm});
            skLineSegment(sketch, "E32.5.2", {"start": v(-106.07, -120.2) * mm, "end": v(-113.14, -127.28) * mm});
            skLineSegment(sketch, "E32.5.3", {"start": v(-81.32, -67.18) * mm, "end": v(-88.39, -74.25) * mm});
            skLineSegment(sketch, "E32.5.4", {"start": v(-74.25, -88.39) * mm, "end": v(-88.39, -74.25) * mm});
            skLineSegment(sketch, "E32.5.5", {"start": v(-74.25, -88.39) * mm, "end": v(-67.18, -81.32) * mm});
            skLineSegment(sketch, "E32.5.6", {"start": v(-127.28, -113.14) * mm, "end": v(-120.2, -106.07) * mm});
            skLineSegment(sketch, "E32.5.7", {"start": v(-81.32, -81.32) * mm, "end": v(-60.1, -60.1) * mm});
            skLineSegment(sketch, "E32.5.8", {"start": v(-113.14, -127.28) * mm, "end": v(-127.28, -113.14) * mm});
            skLineSegment(sketch, "E32.6.0", {"start": v(-51.07, -151.96) * mm, "end": v(-31.75, -157.14) * mm});
            skLineSegment(sketch, "E32.6.1", {"start": v(-17.52, -104.01) * mm, "end": v(-36.84, -98.83) * mm});
            skLineSegment(sketch, "E32.6.2", {"start": v(-31.75, -157.14) * mm, "end": v(-34.34, -166.8) * mm});
            skLineSegment(sketch, "E32.6.3", {"start": v(-36.84, -98.83) * mm, "end": v(-39.42, -108.5) * mm});
            skLineSegment(sketch, "E32.6.4", {"start": v(-20.1, -113.67) * mm, "end": v(-39.42, -108.5) * mm});
            skLineSegment(sketch, "E32.6.5", {"start": v(-20.1, -113.67) * mm, "end": v(-17.52, -104.01) * mm});
            skLineSegment(sketch, "E32.6.6", {"start": v(-53.66, -161.62) * mm, "end": v(-51.07, -151.96) * mm});
            skLineSegment(sketch, "E32.6.7", {"start": v(-29.76, -111.08) * mm, "end": v(-22, -82.1) * mm});
            skLineSegment(sketch, "E32.6.8", {"start": v(-34.34, -166.8) * mm, "end": v(-53.66, -161.62) * mm});
            skLineSegment(sketch, "E32.7.0", {"start": v(31.75, -157.14) * mm, "end": v(51.07, -151.96) * mm});
            skLineSegment(sketch, "E32.7.1", {"start": v(36.84, -98.83) * mm, "end": v(17.52, -104.01) * mm});
            skLineSegment(sketch, "E32.7.2", {"start": v(51.07, -151.96) * mm, "end": v(53.66, -161.62) * mm});
            skLineSegment(sketch, "E32.7.3", {"start": v(17.52, -104.01) * mm, "end": v(20.1, -113.67) * mm});
            skLineSegment(sketch, "E32.7.4", {"start": v(39.42, -108.5) * mm, "end": v(20.1, -113.67) * mm});
            skLineSegment(sketch, "E32.7.5", {"start": v(39.42, -108.5) * mm, "end": v(36.84, -98.83) * mm});
            skLineSegment(sketch, "E32.7.6", {"start": v(34.34, -166.8) * mm, "end": v(31.75, -157.14) * mm});
            skLineSegment(sketch, "E32.7.7", {"start": v(29.76, -111.08) * mm, "end": v(22, -82.1) * mm});
            skLineSegment(sketch, "E32.7.8", {"start": v(53.66, -161.62) * mm, "end": v(34.34, -166.8) * mm});
            skLineSegment(sketch, "E32.8.0", {"start": v(106.07, -120.2) * mm, "end": v(120.2, -106.07) * mm});
            skLineSegment(sketch, "E32.8.1", {"start": v(81.32, -67.18) * mm, "end": v(67.18, -81.32) * mm});
            skLineSegment(sketch, "E32.8.2", {"start": v(120.2, -106.07) * mm, "end": v(127.28, -113.14) * mm});
            skLineSegment(sketch, "E32.8.3", {"start": v(67.18, -81.32) * mm, "end": v(74.25, -88.39) * mm});
            skLineSegment(sketch, "E32.8.4", {"start": v(88.39, -74.25) * mm, "end": v(74.25, -88.39) * mm});
            skLineSegment(sketch, "E32.8.5", {"start": v(88.39, -74.25) * mm, "end": v(81.32, -67.18) * mm});
            skLineSegment(sketch, "E32.8.6", {"start": v(113.14, -127.28) * mm, "end": v(106.07, -120.2) * mm});
            skLineSegment(sketch, "E32.8.7", {"start": v(81.32, -81.32) * mm, "end": v(60.1, -60.1) * mm});
            skLineSegment(sketch, "E32.8.8", {"start": v(127.28, -113.14) * mm, "end": v(113.14, -127.28) * mm});
            skLineSegment(sketch, "E32.9.0", {"start": v(151.96, -51.07) * mm, "end": v(157.14, -31.75) * mm});
            skLineSegment(sketch, "E32.9.1", {"start": v(104.01, -17.52) * mm, "end": v(98.83, -36.84) * mm});
            skLineSegment(sketch, "E32.9.2", {"start": v(157.14, -31.75) * mm, "end": v(166.8, -34.34) * mm});
            skLineSegment(sketch, "E32.9.3", {"start": v(98.83, -36.84) * mm, "end": v(108.5, -39.42) * mm});
            skLineSegment(sketch, "E32.9.4", {"start": v(113.67, -20.1) * mm, "end": v(108.5, -39.42) * mm});
            skLineSegment(sketch, "E32.9.5", {"start": v(113.67, -20.1) * mm, "end": v(104.01, -17.52) * mm});
            skLineSegment(sketch, "E32.9.6", {"start": v(161.62, -53.66) * mm, "end": v(151.96, -51.07) * mm});
            skLineSegment(sketch, "E32.9.7", {"start": v(111.08, -29.76) * mm, "end": v(82.1, -22) * mm});
            skLineSegment(sketch, "E32.9.8", {"start": v(166.8, -34.34) * mm, "end": v(161.62, -53.66) * mm});
            skLineSegment(sketch, "E32.10.0", {"start": v(157.14, 31.75) * mm, "end": v(151.96, 51.07) * mm});
            skLineSegment(sketch, "E32.10.1", {"start": v(98.83, 36.84) * mm, "end": v(104.01, 17.52) * mm});
            skLineSegment(sketch, "E32.10.2", {"start": v(151.96, 51.07) * mm, "end": v(161.62, 53.66) * mm});
            skLineSegment(sketch, "E32.10.3", {"start": v(104.01, 17.52) * mm, "end": v(113.67, 20.1) * mm});
            skLineSegment(sketch, "E32.10.4", {"start": v(108.5, 39.42) * mm, "end": v(113.67, 20.1) * mm});
            skLineSegment(sketch, "E32.10.5", {"start": v(108.5, 39.42) * mm, "end": v(98.83, 36.84) * mm});
            skLineSegment(sketch, "E32.10.6", {"start": v(166.8, 34.34) * mm, "end": v(157.14, 31.75) * mm});
            skLineSegment(sketch, "E32.10.7", {"start": v(111.08, 29.76) * mm, "end": v(82.1, 22) * mm});
            skLineSegment(sketch, "E32.10.8", {"start": v(161.62, 53.66) * mm, "end": v(166.8, 34.34) * mm});
            skLineSegment(sketch, "E32.11.0", {"start": v(120.2, 106.07) * mm, "end": v(106.07, 120.2) * mm});
            skLineSegment(sketch, "E32.11.1", {"start": v(67.18, 81.32) * mm, "end": v(81.32, 67.18) * mm});
            skLineSegment(sketch, "E32.11.2", {"start": v(106.07, 120.2) * mm, "end": v(113.14, 127.28) * mm});
            skLineSegment(sketch, "E32.11.3", {"start": v(81.32, 67.18) * mm, "end": v(88.39, 74.25) * mm});
            skLineSegment(sketch, "E32.11.4", {"start": v(74.25, 88.39) * mm, "end": v(88.39, 74.25) * mm});
            skLineSegment(sketch, "E32.11.5", {"start": v(74.25, 88.39) * mm, "end": v(67.18, 81.32) * mm});
            skLineSegment(sketch, "E32.11.6", {"start": v(127.28, 113.14) * mm, "end": v(120.2, 106.07) * mm});
            skLineSegment(sketch, "E32.11.7", {"start": v(81.32, 81.32) * mm, "end": v(60.1, 60.1) * mm});
            skLineSegment(sketch, "E32.11.8", {"start": v(113.14, 127.28) * mm, "end": v(127.28, 113.14) * mm});
            skSolve(sketch);
        }
        {
            var Q0;
            Q0 = qSketchRegion(id + "F6", true);
            extrude(context, id + "F7", {"entities" : qUnion([Q0]), "operationType" : NewBodyOperationType.REMOVE, "oppositeDirection" : true, "depth" : 1 * mm});
        }
        {
            var Q0;
            Q0=makeQuery(id+"F1.opExtrude","CAP_FACE",FACE,{"disambiguationData":[OSD([sQuery(id+"F0.wireOp",EDGE,"E0.0"),sQuery(id+"F0.wireOp",EDGE,"E0.1"),sQuery(id+"F0.wireOp",EDGE,"E0.2"),sQuery(id+"F0.wireOp",EDGE,"E0.3"),sQuery(id+"F0.wireOp",EDGE,"E0.4"),sQuery(id+"F0.wireOp",EDGE,"E0.5"),sQuery(id+"F0.wireOp",EDGE,"E1"),sQuery(id+"F0.wireOp",EDGE,"E5"),sQuery(id+"F0.wireOp",EDGE,"E6"),sQuery(id+"F0.wireOp",EDGE,"E7.1.0"),sQuery(id+"F0.wireOp",EDGE,"E7.1.1"),sQuery(id+"F0.wireOp",EDGE,"E7.2.0"),sQuery(id+"F0.wireOp",EDGE,"E7.2.1"),sQuery(id+"F0.wireOp",EDGE,"E7.3.0"),sQuery(id+"F0.wireOp",EDGE,"E7.3.1"),sQuery(id+"F0.wireOp",EDGE,"E7.4.0"),sQuery(id+"F0.wireOp",EDGE,"E7.4.1"),sQuery(id+"F0.wireOp",EDGE,"E7.5.0"),sQuery(id+"F0.wireOp",EDGE,"E7.5.1"),sQuery(id+"F0.wireOp",EDGE,"E7.6.0"),sQuery(id+"F0.wireOp",EDGE,"E7.6.1"),sQuery(id+"F0.wireOp",EDGE,"E7.7.0"),sQuery(id+"F0.wireOp",EDGE,"E7.7.1"),sQuery(id+"F0.wireOp",EDGE,"E7.8.0"),sQuery(id+"F0.wireOp",EDGE,"E7.8.1"),sQuery(id+"F0.wireOp",EDGE,"E7.9.0"),sQuery(id+"F0.wireOp",EDGE,"E7.9.1"),sQuery(id+"F0.wireOp",EDGE,"E7.10.0"),sQuery(id+"F0.wireOp",EDGE,"E7.10.1"),sQuery(id+"F0.wireOp",EDGE,"E7.11.0"),sQuery(id+"F0.wireOp",EDGE,"E7.11.1")])],"isStart":true});
            var sketch = newSketch(context, id + "F8", { "sketchPlane" : qUnion([Q0])});
            skCircle(sketch, "E33", {"center": v(0, 0) * mm, "radius": 102.5 * mm});
            skCircle(sketch, "E34", {"center": v(0, 0) * mm, "radius": 117.5 * mm});
            skSolve(sketch);
        }
        {
            var Q0;
            Q0 = qSketchRegion(id + "F8", true);
            extrude(context, id + "F9", {"entities" : qUnion([Q0]), "operationType" : NewBodyOperationType.REMOVE, "oppositeDirection" : true, "depth" : 9.53 * mm});
        }
    });
